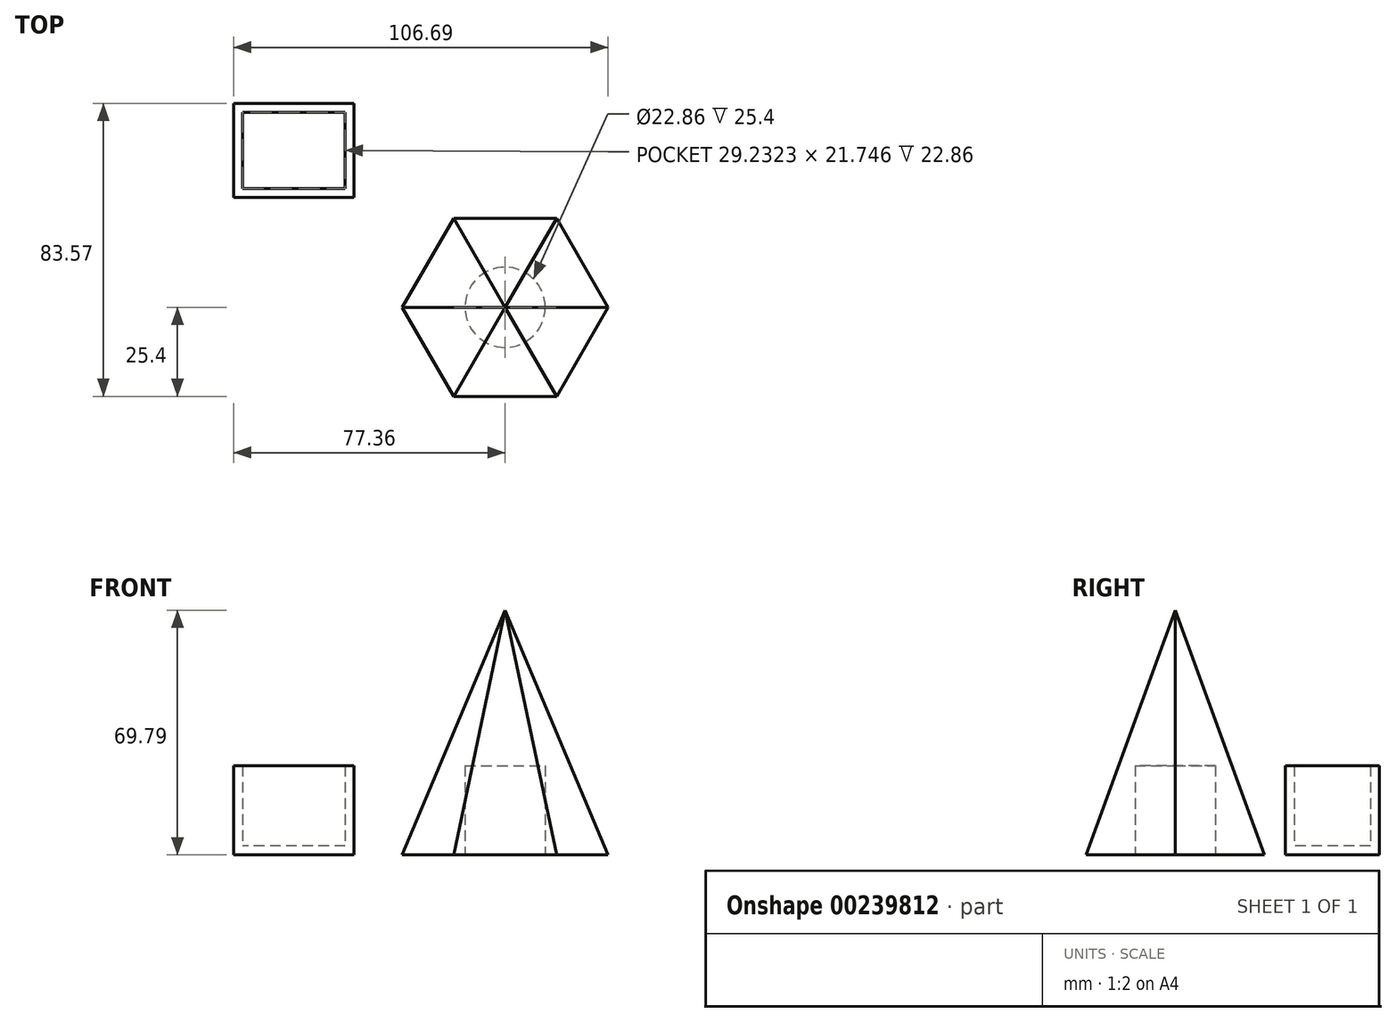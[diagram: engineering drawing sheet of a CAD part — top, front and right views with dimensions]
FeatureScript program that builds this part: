
annotation { "Feature Type Name" : "Feature", "Feature Type Description" : "" }
export const myFeature = defineFeature(function(context is Context, id is Id, definition is map)
    precondition{}
    {
        {
            var Q0;
            Q0=qCreatedBy(makeId("Front.planeOp"),FACE);
            var sketch = newSketch(context, id + "F0", { "sketchPlane" : qUnion([Q0])});
            skLineSegment(sketch, "E0", {"start": v(0, 0) * mm, "end": v(-50.8, 0) * mm});
            skLineSegment(sketch, "E1", {"start": v(-50.8, 0) * mm, "end": v(-50.8, 50.8) * mm});
            skLineSegment(sketch, "E2", {"start": v(-50.8, 50.8) * mm, "end": v(0, 50.8) * mm});
            skLineSegment(sketch, "E3", {"start": v(0, 50.8) * mm, "end": v(0, 0) * mm});
            skSolve(sketch);
        }
        {
            var Q0;
            Q0 = qSketchRegion(id + "F0", true);
            extrude(context, id + "F1", {"entities" : qUnion([Q0]), "endBound" : BoundingType.SYMMETRIC, "oppositeDirection" : true, "depth" : 107.95 * mm});
        }
        {
            var Q0;
            Q0=makeQuery(id+"F1.opExtrude","SWEPT_BODY",BODY,{"disambiguationData":[OSD([sQuery(id+"F0.wireOp",EDGE,"E0"),sQuery(id+"F0.wireOp",EDGE,"E1"),sQuery(id+"F0.wireOp",EDGE,"E2"),sQuery(id+"F0.wireOp",EDGE,"E3")])]});
            deleteBodies(context, id + "F2", {"entities" : qUnion([Q0])});
        }
        {
            var Q0;
            Q0=qCreatedBy(makeId("Top.planeOp"),FACE);
            var sketch = newSketch(context, id + "F3", { "sketchPlane" : qUnion([Q0])});
            skCircle(sketch, "E4.cCircle", {"center": v(0, 0) * mm, "radius": 25.4 * mm, "construction": true});
            skLineSegment(sketch, "E4.0", {"start": v(-14.66, 25.4) * mm, "end": v(14.66, 25.4) * mm});
            skLineSegment(sketch, "E4.1", {"start": v(14.66, 25.4) * mm, "end": v(29.33, 0) * mm});
            skLineSegment(sketch, "E4.2", {"start": v(29.33, 0) * mm, "end": v(14.66, -25.4) * mm});
            skLineSegment(sketch, "E4.3", {"start": v(14.66, -25.4) * mm, "end": v(-14.66, -25.4) * mm});
            skLineSegment(sketch, "E4.4", {"start": v(-14.66, -25.4) * mm, "end": v(-29.33, 0) * mm});
            skLineSegment(sketch, "E4.5", {"start": v(-29.33, 0) * mm, "end": v(-14.66, 25.4) * mm});
            skPoint(sketch, "E4.0.midPoint", {"position": v(0, 25.4) * mm});
            skSolve(sketch);
        }
        {
            var Q0;
            Q0 = qSketchRegion(id + "F3", true);
            extrude(context, id + "F4", {"entities" : qUnion([Q0]), "depth" : 76.2 * mm, "hasDraft" : true, "draftAngle" : 20 * degree, "draftPullDirection" : true});
        }
        {
            var Q0;
            Q0=makeQuery(id+"F4.opExtrude","CAP_FACE",FACE,{"disambiguationData":[OSD([sQuery(id+"F3.wireOp",EDGE,"E4.0"),sQuery(id+"F3.wireOp",EDGE,"E4.1"),sQuery(id+"F3.wireOp",EDGE,"E4.2"),sQuery(id+"F3.wireOp",EDGE,"E4.3"),sQuery(id+"F3.wireOp",EDGE,"E4.4"),sQuery(id+"F3.wireOp",EDGE,"E4.5")])],"isStart":true});
            var sketch = newSketch(context, id + "F5", { "sketchPlane" : qUnion([Q0])});
            skCircle(sketch, "E5", {"center": v(0, 0) * mm, "radius": 11.43 * mm});
            skSolve(sketch);
        }
        {
            var Q0;
            Q0 = qSketchRegion(id + "F5", true);
            extrude(context, id + "F6", {"entities" : qUnion([Q0]), "operationType" : NewBodyOperationType.REMOVE, "oppositeDirection" : true, "depth" : 25.4 * mm});
        }
        {
            var Q0;
            Q0=qCreatedBy(makeId("Top.planeOp"),FACE);
            var sketch = newSketch(context, id + "F7", { "sketchPlane" : qUnion([Q0])});
            skLineSegment(sketch, "E6.bottom", {"start": v(-43.05, 58.17) * mm, "end": v(-77.36, 58.17) * mm});
            skLineSegment(sketch, "E6.top", {"start": v(-43.05, 31.35) * mm, "end": v(-77.36, 31.35) * mm});
            skLineSegment(sketch, "E6.left", {"start": v(-43.05, 58.17) * mm, "end": v(-43.05, 31.35) * mm});
            skLineSegment(sketch, "E6.right", {"start": v(-77.36, 58.17) * mm, "end": v(-77.36, 31.35) * mm});
            skPoint(sketch, "E6.middle", {"position": v(-60.2, 44.76) * mm});
            skSolve(sketch);
        }
        {
            var Q0;
            Q0 = qSketchRegion(id + "F7", true);
            extrude(context, id + "F8", {"entities" : qUnion([Q0]), "depth" : 25.4 * mm});
        }
        {
            var Q0;
            Q0=makeQuery(id+"F8.opExtrude","CAP_FACE",FACE,{"disambiguationData":[OSD([sQuery(id+"F7.wireOp",EDGE,"E6.bottom"),sQuery(id+"F7.wireOp",EDGE,"E6.top"),sQuery(id+"F7.wireOp",EDGE,"E6.left"),sQuery(id+"F7.wireOp",EDGE,"E6.right")])],"isStart":false});
            shell(context, id + "F9", {"entities" : qUnion([Q0]), "thickness" : 2.54 * mm});
        }
    });
